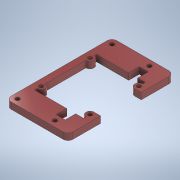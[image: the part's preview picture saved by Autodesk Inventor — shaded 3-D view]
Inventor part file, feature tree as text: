
AUTODESK INVENTOR PART (.ipt)
format: ipt  version: 2021 (Build 250183000, 183)  size: 201,728 bytes
history: native  units: mm
features: extrude x1, fillet x1, sketch x1
ambient origin geometry x8: Origin, YZ Plane, XZ Plane, XY Plane, X Axis, Y Axis, Z Axis, Center Point
bodies: Solid1 (feature_tree)
feature tree (3):
  extrude  "Extrusion1"  Depth=38.0mm
  fillet  "Fillet1"  Radius=38.0mm
  sketch  "Sketch1"  dims[d0=38.0mm d2=38.0mm d3=38.0mm d4=30.0mm d8=65.0mm d9=23.0mm d10=58.0mm d11=3.5mm d13=3.5mm d14=2.5mm d15=2.5mm d16=2.5mm d17=2.5mm d18=2.5mm d19=2.5mm d20=2.5mm d21=2.5mm d22=5.0mm d23=5.0mm d24=7.0mm d25=7.0mm d28=4.0mm d29=0.0mm d30=3.0mm d31=5.0mm d32=5.0mm d33=4.0mm d34=5.0mm d35=5.0mm d36=5.5mm d37=51.0mm]
